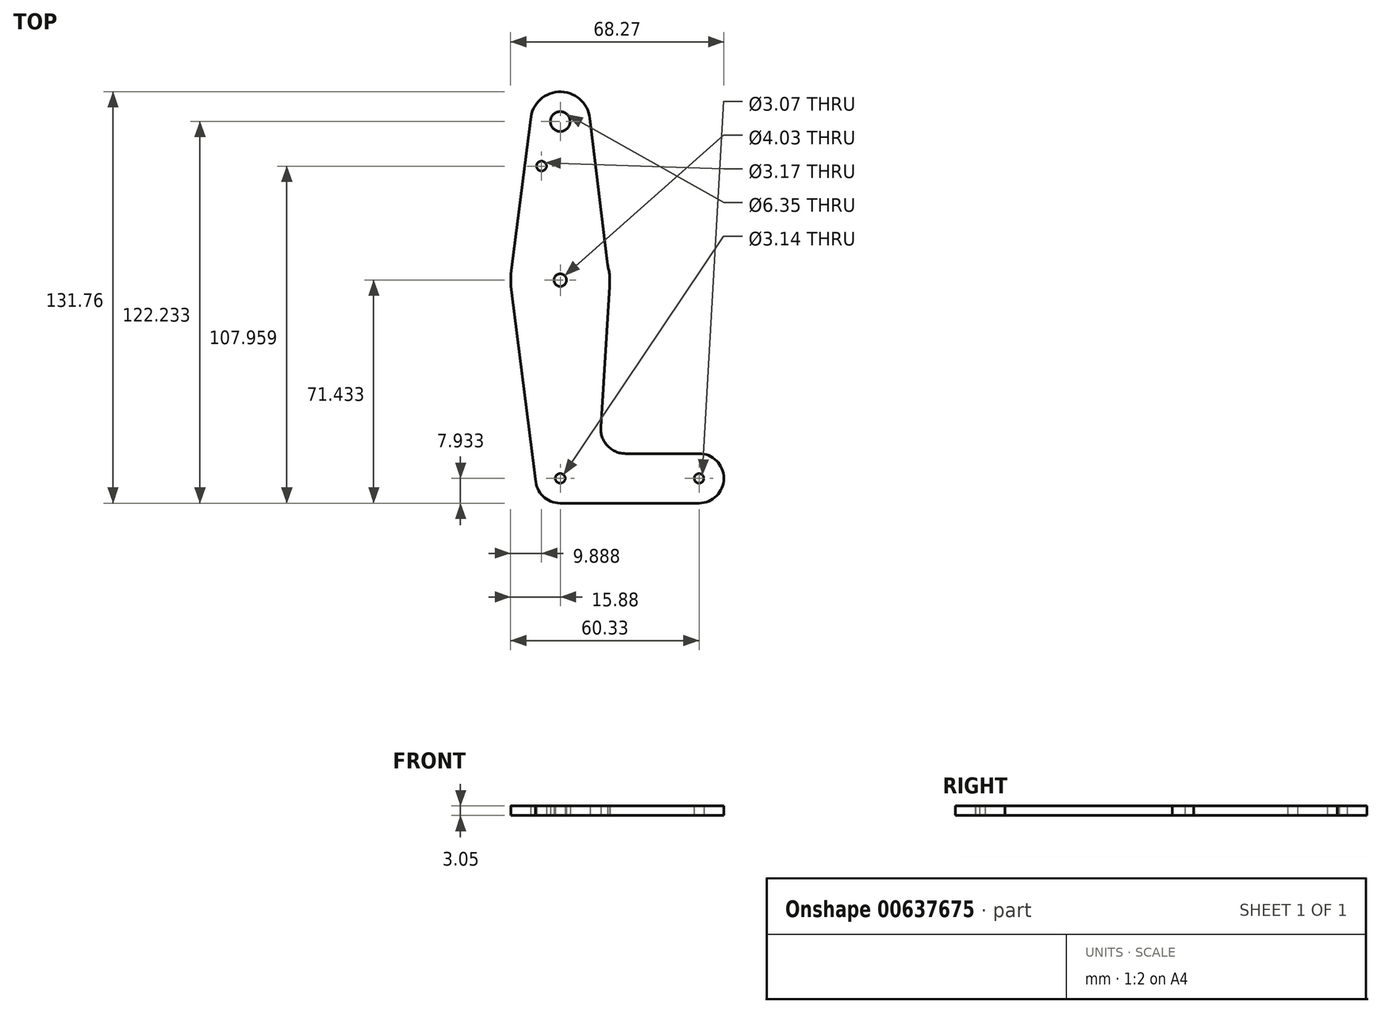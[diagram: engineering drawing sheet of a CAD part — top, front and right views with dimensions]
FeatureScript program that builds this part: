
annotation { "Feature Type Name" : "Feature", "Feature Type Description" : "" }
export const myFeature = defineFeature(function(context is Context, id is Id, definition is map)
    precondition{}
    {
        {
            var Q0;
            Q0=qCreatedBy(makeId("Top.planeOp"),FACE);
            var sketch = newSketch(context, id + "F0", { "sketchPlane" : qUnion([Q0])});
            skLineSegment(sketch, "E0", {"start": v(-44.45, 134.04) * mm, "end": v(-44.45, 19.74) * mm, "construction": true});
            skLineSegment(sketch, "E1", {"start": v(-44.45, 19.74) * mm, "end": v(0, 19.74) * mm, "construction": true});
            skCircle(sketch, "E2", {"center": v(-44.45, 134.04) * mm, "radius": 9.53 * mm});
            skCircle(sketch, "E3", {"center": v(-44.45, 83.24) * mm, "radius": 15.88 * mm});
            skCircle(sketch, "E4", {"center": v(-44.45, 19.74) * mm, "radius": 7.94 * mm});
            skCircle(sketch, "E5", {"center": v(0, 19.74) * mm, "radius": 7.94 * mm});
            skLineSegment(sketch, "E6", {"start": v(-34.93, 134.04) * mm, "end": v(-29.34, 88.1) * mm});
            skLineSegment(sketch, "E7", {"start": v(-53.96, 134.65) * mm, "end": v(-60.2, 85.23) * mm});
            skLineSegment(sketch, "E8", {"start": v(-44.45, 27.68) * mm, "end": v(-44.45, 27.68) * mm});
            skLineSegment(sketch, "E9", {"start": v(-52.38, 19.46) * mm, "end": v(-60.2, 81.25) * mm});
            skCircle(sketch, "E10", {"center": v(-50.44, 119.77) * mm, "radius": 1.59 * mm});
            skLineSegment(sketch, "E11.trimOffspring", {"start": v(-23.53, 27.68) * mm, "end": v(0, 27.68) * mm});
            skPoint(sketch, "E12.visualSharp", {"position": v(-31.75, 27.68) * mm});
            skArc(sketch, "E12.filletArc", {"start": v(-31.47, 36.12) * mm, "mid": v(-29.32, 30.18) * mm, "end": v(-23.53, 27.68) * mm});
            skLineSegment(sketch, "E13", {"start": v(-31.47, 36.12) * mm, "end": v(-28.7, 81.25) * mm});
            skLineSegment(sketch, "E14", {"start": v(-44.5, 11.8) * mm, "end": v(0, 11.8) * mm});
            skCircle(sketch, "E15", {"center": v(-44.45, 134.04) * mm, "radius": 3.18 * mm});
            skCircle(sketch, "E16", {"center": v(-44.45, 134.04) * mm, "radius": 0.95 * mm});
            skCircle(sketch, "E17", {"center": v(-44.45, 83.24) * mm, "radius": 2.01 * mm});
            skCircle(sketch, "E18", {"center": v(-44.45, 19.74) * mm, "radius": 1.57 * mm});
            skCircle(sketch, "E19", {"center": v(0, 19.74) * mm, "radius": 1.53 * mm});
            skSolve(sketch);
        }
        {
            var Q0;
            Q0=makeQuery(id+"F0.imprint","IMPRINT",FACE,{"disambiguationData":[TD([[makeQuery(id+"F0.imprint","IMPRINT",EDGE,{"derivedFrom":sQuery(id+"F0.wireOp",EDGE,"E15")}),-1.0]])]});
            var Q1;
            {var subQ0=sQuery(id+"F0.wireOp",EDGE,"E6");Q1=makeQuery(id+"F0.imprint","IMPRINT",FACE,{"disambiguationData":[TD([[makeQuery(id+"F0.imprint","IMPRINT",EDGE,{"derivedFrom":subQ0}),-1.0]])]});}
            var Q2;
            Q2=makeQuery(id+"F0.imprint","IMPRINT",FACE,{"disambiguationData":[TD([[makeQuery(id+"F0.imprint","IMPRINT",EDGE,{"derivedFrom":sQuery(id+"F0.wireOp",EDGE,"E17")}),-1.0]])]});
            var Q3;
            {var subQ3=sQuery(id+"F0.wireOp",EDGE,"E9");Q3=makeQuery(id+"F0.imprint","IMPRINT",FACE,{"disambiguationData":[TD([[makeQuery(id+"F0.imprint","IMPRINT",EDGE,{"derivedFrom":subQ3}),-1.0]])]});}
            var Q4;
            Q4=makeQuery(id+"F0.imprint","IMPRINT",FACE,{"disambiguationData":[TD([[makeQuery(id+"F0.imprint","IMPRINT",EDGE,{"derivedFrom":sQuery(id+"F0.wireOp",EDGE,"E19")}),-1.0]])]});
            var Q5;
            Q5=makeQuery(id+"F0.imprint","IMPRINT",FACE,{"disambiguationData":[TD([[makeQuery(id+"F0.imprint","IMPRINT",EDGE,{"derivedFrom":sQuery(id+"F0.wireOp",EDGE,"E18")}),-1.0]])]});
            extrude(context, id + "F1", {"entities" : qUnion([Q0, Q1, Q2, Q3, Q4, Q5]), "depth" : 3.05 * mm, "offsetDistance" : 25.4 * mm});
        }
    });
